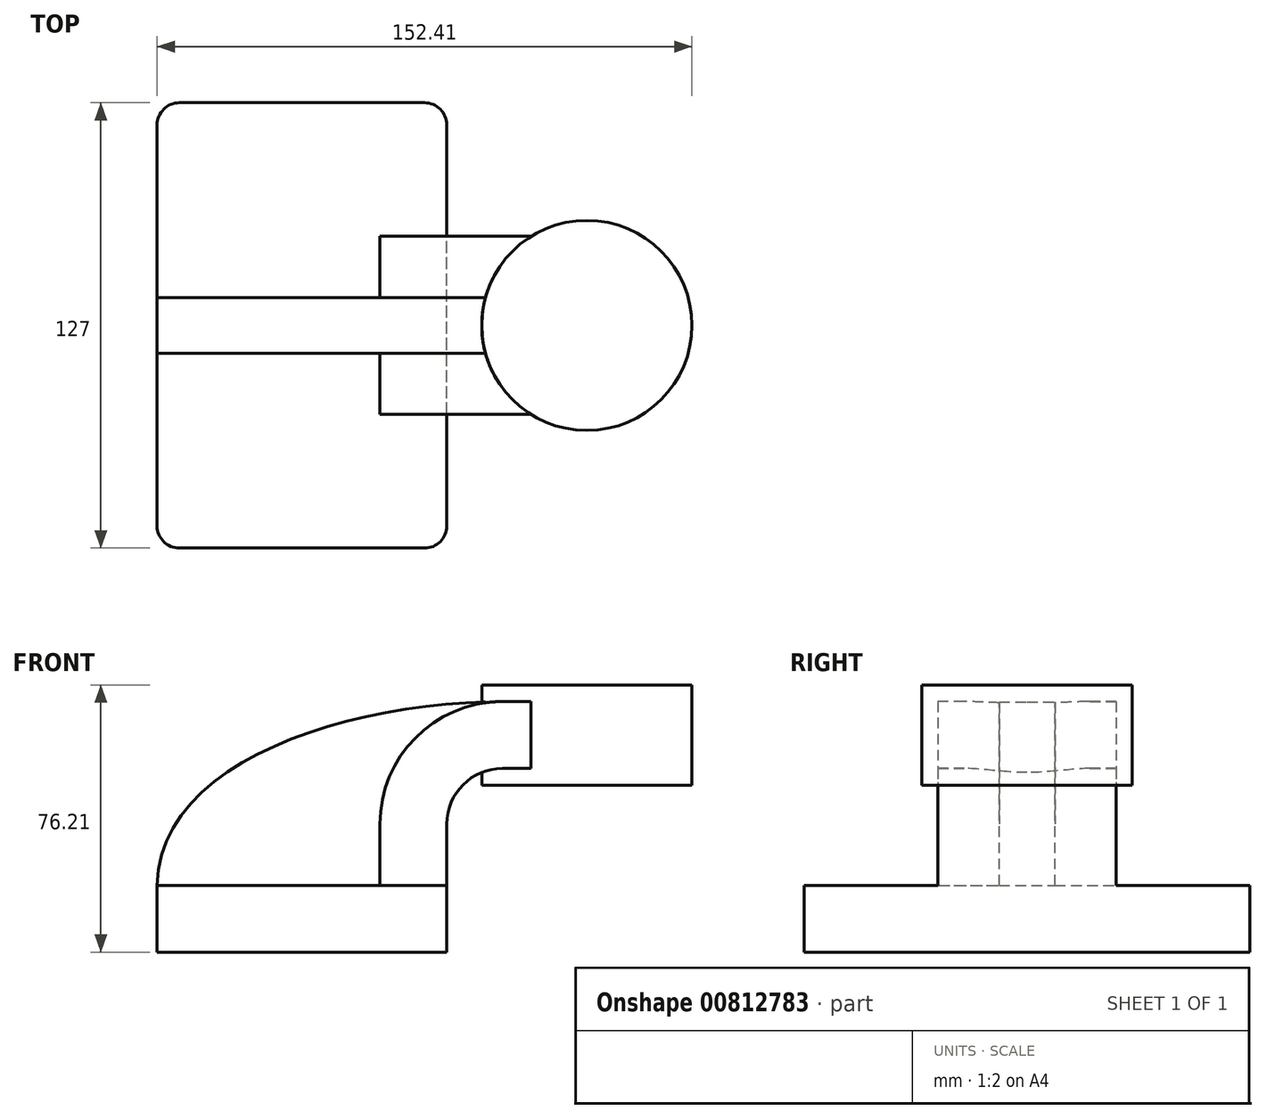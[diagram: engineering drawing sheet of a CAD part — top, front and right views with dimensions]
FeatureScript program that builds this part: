
annotation { "Feature Type Name" : "Feature", "Feature Type Description" : "" }
export const myFeature = defineFeature(function(context is Context, id is Id, definition is map)
    precondition{}
    {
        {
            var Q0;
            Q0=qCreatedBy(makeId("Front.planeOp"),FACE);
            var sketch = newSketch(context, id + "F0", { "sketchPlane" : qUnion([Q0])});
            skLineSegment(sketch, "E0.bottom", {"start": v(-41.28, -9.53) * mm, "end": v(41.28, -9.53) * mm});
            skLineSegment(sketch, "E0.top", {"start": v(-41.28, 9.52) * mm, "end": v(41.28, 9.52) * mm});
            skLineSegment(sketch, "E0.left", {"start": v(-41.28, -9.53) * mm, "end": v(-41.28, 9.52) * mm});
            skLineSegment(sketch, "E0.right", {"start": v(41.28, -9.53) * mm, "end": v(41.28, 9.52) * mm});
            skPoint(sketch, "E0.middle", {"position": v(0, 0) * mm});
            skLineSegment(sketch, "E1.bottom", {"start": v(60.32, 66.67) * mm, "end": v(111.12, 66.67) * mm});
            skLineSegment(sketch, "E1.top", {"start": v(60.32, 38.1) * mm, "end": v(111.12, 38.1) * mm});
            skLineSegment(sketch, "E1.left", {"start": v(60.32, 66.67) * mm, "end": v(60.32, 38.1) * mm});
            skLineSegment(sketch, "E1.right", {"start": v(111.12, 66.67) * mm, "end": v(111.12, 38.1) * mm});
            skPoint(sketch, "E1.middle", {"position": v(85.72, 52.39) * mm});
            skLineSegment(sketch, "E2", {"start": v(41.27, 9.52) * mm, "end": v(41.27, 26.99) * mm});
            skArc(sketch, "E3", {"start": v(41.27, 26.99) * mm, "mid": v(45.92, 38.21) * mm, "end": v(57.15, 42.86) * mm});
            skLineSegment(sketch, "E4", {"start": v(57.15, 42.86) * mm, "end": v(81.17, 42.86) * mm});
            skLineSegment(sketch, "E5.0", {"start": v(57.15, 61.91) * mm, "end": v(81.17, 61.91) * mm});
            skArc(sketch, "E5.1", {"start": v(22.22, 26.99) * mm, "mid": v(32.45, 51.68) * mm, "end": v(57.15, 61.91) * mm});
            skLineSegment(sketch, "E5.2", {"start": v(22.22, 9.52) * mm, "end": v(22.22, 26.99) * mm});
            skFitSpline(sketch, "E6", {"points": [v(-41.28, 9.53) * mm, v(57.15, 61.91) * mm], "startDerivative": vector(1.9, 107.02) * mm, "endDerivative": vector(131.45, 0.7) * mm});
            skPoint(sketch, "E7.endSnap0", {"position": v(85.72, 66.67) * mm});
            skLineSegment(sketch, "E8", {"start": v(81.17, 38.1) * mm, "end": v(81.17, 52.73) * mm});
            skLineSegment(sketch, "E9", {"start": v(81.17, 52.73) * mm, "end": v(81.17, 61.91) * mm});
            skLineSegment(sketch, "E10", {"start": v(81.17, 61.91) * mm, "end": v(81.17, 66.67) * mm});
            skSolve(sketch);
        }
        {
            var Q0;
            Q0=makeQuery(id+"F0.imprint","IMPRINT",FACE,{"disambiguationData":[TD([[makeQuery(id+"F0.imprint","IMPRINT",EDGE,{"derivedFrom":sQuery(id+"F0.wireOp",EDGE,"E0.bottom")}),1.0]])]});
            extrude(context, id + "F1", {"entities" : qUnion([Q0]), "endBound" : BoundingType.SYMMETRIC, "depth" : 127 * mm, "offsetDistance" : 25.4 * mm});
        }
        {
            var Q0;
            {var subQ0=sQuery(id+"F0.wireOp",EDGE,"E2");Q0=makeQuery(id+"F0.imprint","IMPRINT",FACE,{"disambiguationData":[TD([[makeQuery(id+"F0.imprint","IMPRINT",EDGE,{"derivedFrom":subQ0}),1.0]])]});}
            var Q1;
            {var subQ5=sQuery(id+"F0.wireOp",EDGE,"nOBMLaaL-bkRm-sddV-X3qO-CVSsPb6DesUQ");Q1=makeQuery(id+"F0.imprint","IMPRINT",FACE,{"disambiguationData":[TD([[makeQuery(id+"F0.imprint","IMPRINT",EDGE,{"derivedFrom":subQ5}),1.0]])]});}
            extrude(context, id + "F2", {"entities" : qUnion([Q0, Q1]), "operationType" : NewBodyOperationType.ADD, "endBound" : BoundingType.SYMMETRIC, "depth" : 50.8 * mm, "offsetDistance" : 25.4 * mm});
        }
        {
            var Q0;
            {var subQ3=sQuery(id+"F0.wireOp",EDGE,"E5.2");Q0=makeQuery(id+"F0.imprint","IMPRINT",FACE,{"disambiguationData":[TD([[makeQuery(id+"F0.imprint","IMPRINT",EDGE,{"derivedFrom":subQ3}),1.0]])]});}
            extrude(context, id + "F3", {"entities" : qUnion([Q0]), "operationType" : NewBodyOperationType.ADD, "endBound" : BoundingType.SYMMETRIC, "depth" : 15.88 * mm, "offsetDistance" : 25.4 * mm});
        }
        {
            var Q0;
            {var subQ0=sQuery(id+"F0.wireOp",EDGE,"E9");Q0=makeQuery(id+"F0.imprint","IMPRINT",FACE,{"disambiguationData":[TD([[makeQuery(id+"F0.imprint","IMPRINT",EDGE,{"derivedFrom":subQ0}),1.0]])]});}
            extrude(context, id + "F4", {"entities" : qUnion([Q0]), "operationType" : NewBodyOperationType.ADD, "endBound" : BoundingType.SYMMETRIC, "depth" : 50.8 * mm, "offsetDistance" : 25.4 * mm});
        }
        {
            var Q0;
            {var subQ4=sQuery(id+"F0.wireOp",EDGE,"E1.right");Q0=makeQuery(id+"F0.imprint","IMPRINT",FACE,{"disambiguationData":[TD([[makeQuery(id+"F0.imprint","IMPRINT",EDGE,{"derivedFrom":subQ4}),-1.0]])]});}
            var Q1;
            Q1=sQuery(id+"F0.wireOp",EDGE,"E9");
            revolve(context, id + "F5", {"operationType" : NewBodyOperationType.ADD, "surfaceOperationType" : NewSurfaceOperationType.NEW, "entities" : qUnion([Q0]), "axis" : qUnion([Q1]), "revolveType" : RevolveType.FULL});
        }
        {
            var Q0;
            Q0=makeQuery(id+"F1.opExtrude","CAP_EDGE",EDGE,{"disambiguationData":[OSD([sQuery(id+"F0.wireOp",EDGE,"E0.left")])],"isStart":false});
            var Q1;
            Q1=makeQuery(id+"F1.opExtrude","CAP_EDGE",EDGE,{"disambiguationData":[OSD([sQuery(id+"F0.wireOp",EDGE,"E0.right")])],"isStart":false});
            var Q2;
            Q2=makeQuery(id+"F1.opExtrude","CAP_EDGE",EDGE,{"disambiguationData":[OSD([sQuery(id+"F0.wireOp",EDGE,"E0.right")])],"isStart":true});
            var Q3;
            Q3=makeQuery(id+"F1.opExtrude","CAP_EDGE",EDGE,{"disambiguationData":[OSD([sQuery(id+"F0.wireOp",EDGE,"E0.left")])],"isStart":true});
            fillet(context, id + "F6", {"entities" : qUnion([Q0, Q1, Q2, Q3]), "radius" : 6.35 * mm, "tangentPropagation" : true, "allowEdgeOverflow" : false});
        }
    });
